# Revit family: sh-230M-12v
name_source: partatom
category: Lighting Fixtures
revit_build: Autodesk Revit 2017 (Build: 20160225_1515(x64)
units: mm (PartAtom-declared; Revit-internal decimal feet)

## family parameters
Always vertical = Yes
Cut with Voids When Loaded = No
Host = Ceiling
Light Source = Yes
OmniClass Number = 23.80.70.11
OmniClass Title = Luminaries for Internal Lighting
Part Type = Normal
Room Calculation Point = No
Round Connector Dimension = Use Diameter
Shared = No

## types (2) — shared parameters
Body Material = ABS
Body color = White Body
Color Filter = 16777215
Default Elevation = 0.0 cm
Dimming Lamp Color Temperature Shift = <None>
Emit Shape Visible in Rendering = No
Emit from Circle Diameter = 3.0 cm
Flicker = Free Flicker
IP = IP65
Lamp = LED
Manufacturer = SHOA
Model = Sh-230M-12v
Photometric Web File = SH 230M.ies
Protection Class = Class II
Tilt Angle = 90.00°
Type medule = SMD
URL = https://www.shoaco.com
Voltage/Frequency = 12V-DC
Wattage. = 12 W
Width = 10.5 cm
color rendering index(CRI) = 80
color temperature = 4000K
consumption current = 1 A
instalation = Surface Mounted
website = www.shoaco.com

## type names (no varying parameters)
- SH-230M-ND(Black body-4000K-LED)
- SH-230M-ND(white body-4000K-LED)

## geometry (parser evidence)
native form markers: Sweep x1
no freeform markers — native parametric forms only
